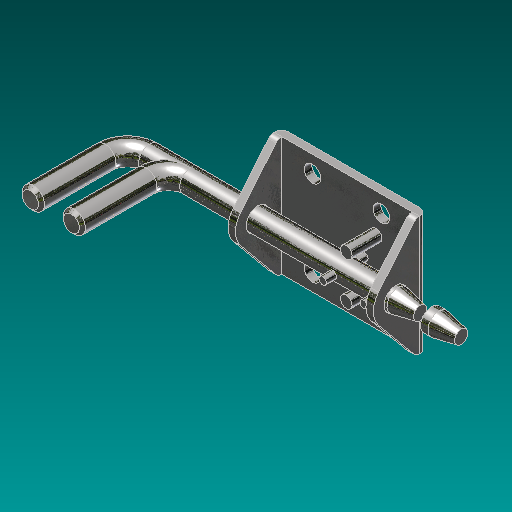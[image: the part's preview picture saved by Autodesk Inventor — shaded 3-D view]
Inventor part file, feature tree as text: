
AUTODESK INVENTOR PART (.ipt)
format: ipt  version: 2017 (Build 210142000, 142)  size: 282,624 bytes
history: native  units: in
note: dims shown in document units (in); Inventor stores cm internally (conversion verified against a paired STEP export)
features: sketch x8, extrude x5, chamfer x3, hole x2, shell x1, fillet x1, sweep x1, plane x1, pattern_linear x1, other x1
ambient origin geometry x8: Origin, YZ Plane, XZ Plane, XY Plane, X Axis, Y Axis, Z Axis, Center Point
bodies: Solid1 (feature_tree)
feature tree (24):
  extrude  "Extrusion1"  Depth=2.0in
  extrude  "Extrusion2"  Depth=0.125in
  shell  "Shell1"  Thickness=0.125in
  fillet  "Fillet1"  Radius=0.9in
  hole  "Hole1"  [1 undecoded]
  hole  "Hole2"  [1 undecoded]
  sweep  "Sweep1"
  chamfer  "Chamfer1"  Distance=1.1in
  chamfer  "Chamfer2"  Distance=1.375in
  extrude  "Extrusion3"  Depth=0.6875in
  plane  "Work Plane1"
  extrude  "Extrusion4"  Depth=0.6875in
  pattern_linear  "Rectangular Pattern1"  Spacing1=0.371in  [1 undecoded]
  extrude  "Extrusion5"  TaperAngle=0.0deg  [1 undecoded]
  chamfer  "Chamfer3"  Distance=0.05in Angle=45.0deg
  sketch  "Sketch1"  dims[d0=2.4375in d1=2.0in]
  sketch  "Sketch2"  dims[d2=1.0in d3=0.0in d4=0.125in d5=0.125in d6=0.9in]
  sketch  "Sketch3"  dims[d7=0.375in d8=1.0in d9=0.0in]
  sketch  "Sketch4"  dims[d10=0.125in d11=0.125in]
  sketch  "Sketch5"  dims[d12=1.0in d13=1.0in]
  sketch  "Sketch6"  dims[d14=0.3906in d15=0.75in d16=0.375in d17=0.25in d18=0.5635in d19=1.0in d20=0.8108in d21=1.1562in]
  other  "Work Axis1"
  sketch  "Sketch7"  dims[d22=1.4375in]
  sketch  "Sketch8"  dims[d23=0.277in d24=0.75in d25=0.375in d26=0.25in d27=0.5635in d28=1.0in d29=0.8108in d30=1.1in d31=1.375in d32=0.375in d33=1.625in d34=0.371in d35=0.0in d36=0.05in d37=0.125in d38=45.0deg d39=0.375in d40=0.125in d41=0.0756in d42=0.1969in d44=0.506in d45=0.7188in d46=0.5in d47=0.0in d48=0.0in d49=0.125in d50=0.7in d51=0.0in d52=0.7874in d54=0.6875in d55=0.5in d56=0.6875in d57=0.7in d58=0.0in d59=0.375in d60=0.125in d61=0.0756in d62=0.0in]
note: 4 required parameter values undecoded (feature->parameter linkage not recoverable at this tier; creation-order binding heuristic only, values carry confidence <= 0.55)
